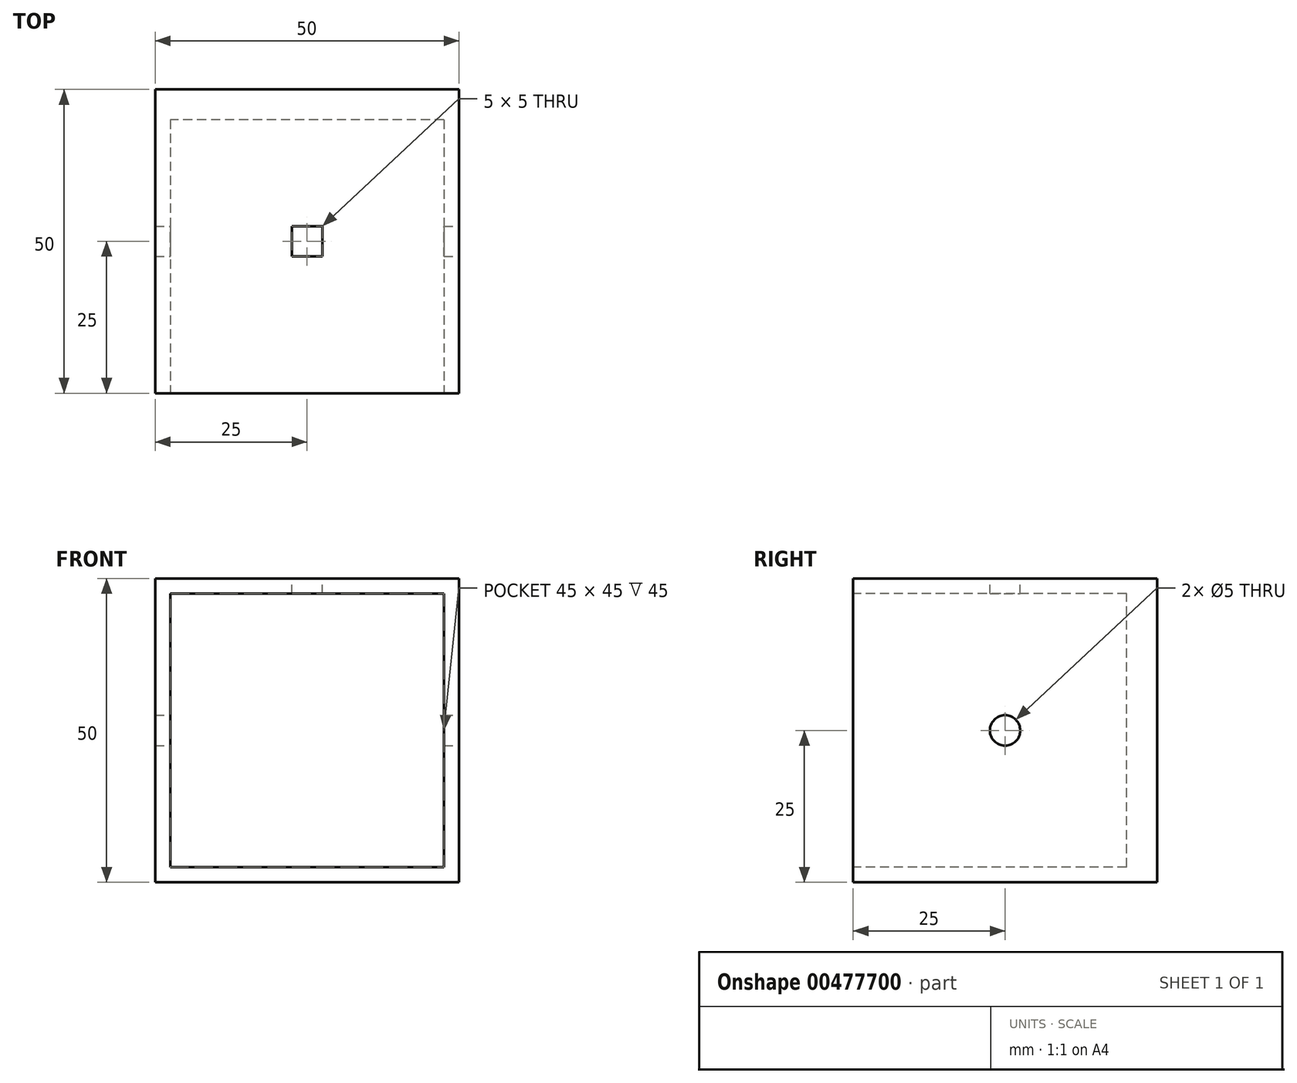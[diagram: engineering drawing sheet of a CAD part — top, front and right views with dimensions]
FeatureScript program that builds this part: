
annotation { "Feature Type Name" : "Feature", "Feature Type Description" : "" }
export const myFeature = defineFeature(function(context is Context, id is Id, definition is map)
    precondition{}
    {
        {
            var Q0;
            Q0=qCreatedBy(makeId("Top.planeOp"),FACE);
            var sketch = newSketch(context, id + "F0", { "sketchPlane" : qUnion([Q0])});
            skLineSegment(sketch, "E0.bottom", {"start": v(25, 25) * mm, "end": v(-25, 25) * mm});
            skLineSegment(sketch, "E0.top", {"start": v(25, -25) * mm, "end": v(-25, -25) * mm});
            skLineSegment(sketch, "E0.left", {"start": v(25, 25) * mm, "end": v(25, -25) * mm});
            skLineSegment(sketch, "E0.right", {"start": v(-25, 25) * mm, "end": v(-25, -25) * mm});
            skPoint(sketch, "E0.middle", {"position": v(0, 0) * mm});
            skSolve(sketch);
        }
        {
            var Q0;
            Q0 = qSketchRegion(id + "F0", true);
            var Q1;
            Q1=makeQuery(id+"F0.imprint","IMPRINT",FACE,{"disambiguationData":[TD([[makeQuery(id+"F0.imprint","IMPRINT",EDGE,{"derivedFrom":sQuery(id+"F0.wireOp",EDGE,"E0.bottom")}),1.0]])]});
            extrude(context, id + "F1", {"entities" : qUnion([Q0, Q1]), "depth" : 25 * mm, "hasSecondDirection" : true, "secondDirectionOppositeDirection" : true, "secondDirectionDepth" : 25 * mm});
        }
        {
            var Q0;
            Q0=makeQuery(id+"F1.opExtrude","SWEPT_FACE",FACE,{"disambiguationData":[OSD([sQuery(id+"F0.wireOp",EDGE,"E0.top")])]});
            var sketch = newSketch(context, id + "F2", { "sketchPlane" : qUnion([Q0])});
            skLineSegment(sketch, "E1.bottom", {"start": v(22.5, -22.5) * mm, "end": v(-22.5, -22.5) * mm});
            skLineSegment(sketch, "E1.top", {"start": v(22.5, 22.5) * mm, "end": v(-22.5, 22.5) * mm});
            skLineSegment(sketch, "E1.left", {"start": v(22.5, -22.5) * mm, "end": v(22.5, 22.5) * mm});
            skLineSegment(sketch, "E1.right", {"start": v(-22.5, -22.5) * mm, "end": v(-22.5, 22.5) * mm});
            skPoint(sketch, "E1.middle", {"position": v(0, 0) * mm});
            skSolve(sketch);
        }
        {
            var Q0;
            Q0=makeQuery(id+"F2.imprint","IMPRINT",FACE,{"disambiguationData":[TD([[makeQuery(id+"F2.imprint","IMPRINT",EDGE,{"derivedFrom":sQuery(id+"F2.wireOp",EDGE,"E1.bottom")}),-1.0]])]});
            extrude(context, id + "F3", {"entities" : qUnion([Q0]), "operationType" : NewBodyOperationType.REMOVE, "oppositeDirection" : true, "depth" : 45 * mm});
        }
        {
            var Q0;
            Q0=makeQuery(id+"F1.opExtrude","CAP_FACE",FACE,{"disambiguationData":[OSD([sQuery(id+"F0.wireOp",EDGE,"E0.bottom"),sQuery(id+"F0.wireOp",EDGE,"E0.top"),sQuery(id+"F0.wireOp",EDGE,"E0.left"),sQuery(id+"F0.wireOp",EDGE,"E0.right")])],"isStart":false});
            var sketch = newSketch(context, id + "F4", { "sketchPlane" : qUnion([Q0])});
            skLineSegment(sketch, "E2.bottom", {"start": v(2.5, -2.5) * mm, "end": v(-2.5, -2.5) * mm});
            skLineSegment(sketch, "E2.top", {"start": v(2.5, 2.5) * mm, "end": v(-2.5, 2.5) * mm});
            skLineSegment(sketch, "E2.left", {"start": v(2.5, -2.5) * mm, "end": v(2.5, 2.5) * mm});
            skLineSegment(sketch, "E2.right", {"start": v(-2.5, -2.5) * mm, "end": v(-2.5, 2.5) * mm});
            skPoint(sketch, "E2.middle", {"position": v(0, 0) * mm});
            skSolve(sketch);
        }
        {
            var Q0;
            Q0=makeQuery(id+"F4.imprint","IMPRINT",FACE,{"disambiguationData":[TD([[makeQuery(id+"F4.imprint","IMPRINT",EDGE,{"derivedFrom":sQuery(id+"F4.wireOp",EDGE,"E2.bottom")}),-1.0]])]});
            extrude(context, id + "F5", {"entities" : qUnion([Q0]), "operationType" : NewBodyOperationType.REMOVE, "oppositeDirection" : true, "depth" : 5 * mm});
        }
        {
            var Q0;
            Q0=qCreatedBy(makeId("Right.planeOp"),FACE);
            var sketch = newSketch(context, id + "F6", { "sketchPlane" : qUnion([Q0])});
            skCircle(sketch, "E3", {"center": v(0, 0) * mm, "radius": 2.5 * mm});
            skSolve(sketch);
        }
        {
            var Q0;
            Q0 = qSketchRegion(id + "F6", true);
            extrude(context, id + "F7", {"entities" : qUnion([Q0]), "operationType" : NewBodyOperationType.REMOVE, "oppositeDirection" : true, "depth" : 50 * mm, "hasSecondDirection" : true, "secondDirectionOppositeDirection" : false, "secondDirectionDepth" : 25 * mm});
        }
    });
